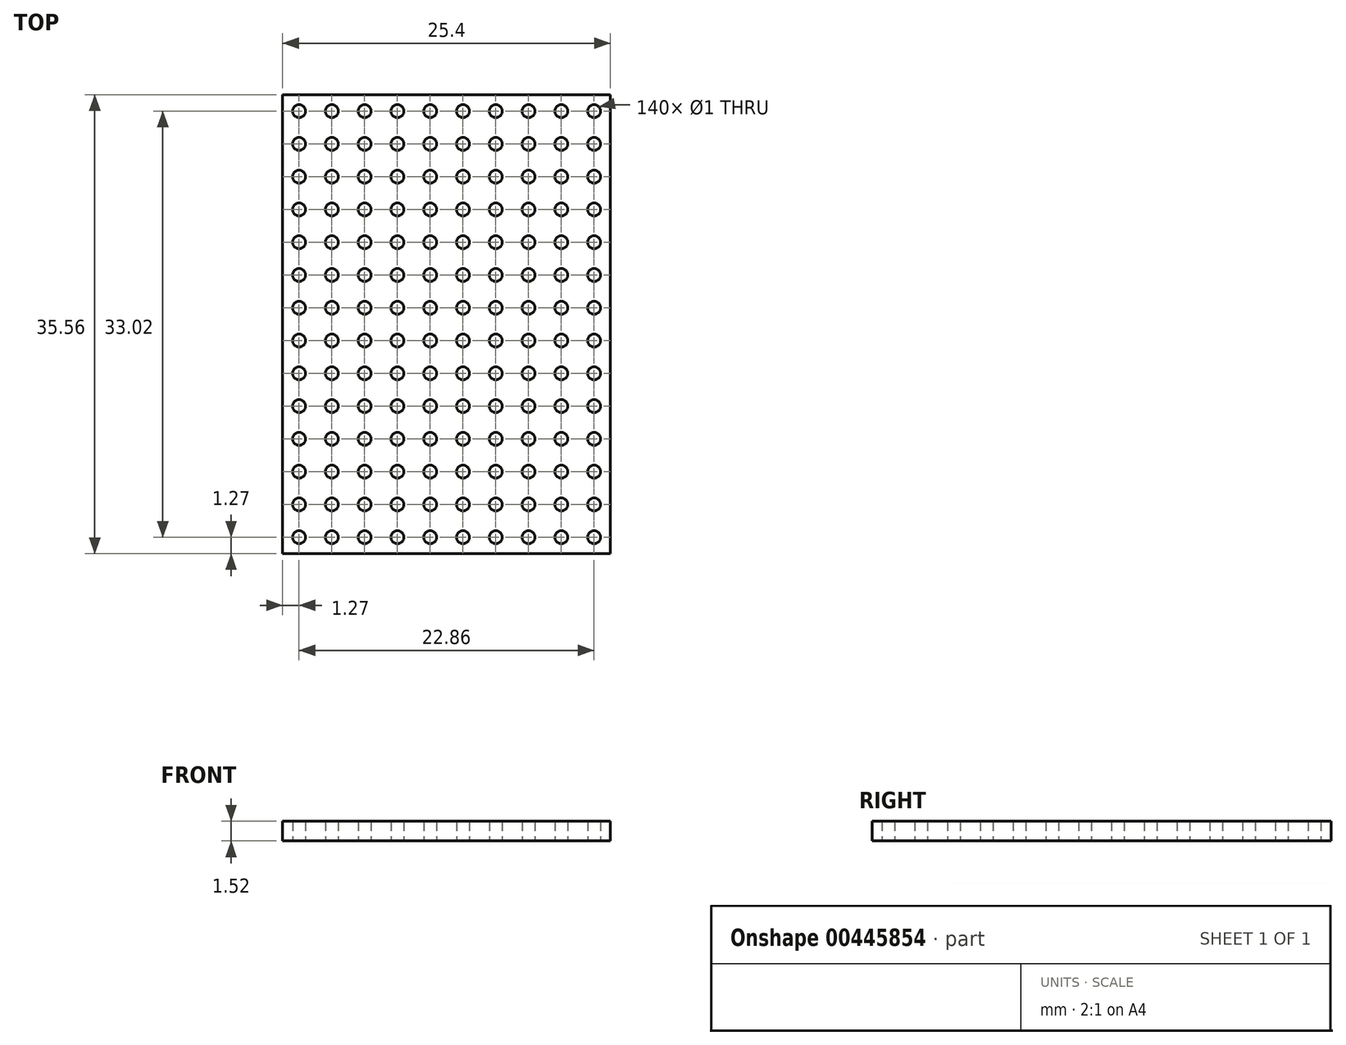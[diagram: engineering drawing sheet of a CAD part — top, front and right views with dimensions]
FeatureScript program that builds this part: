
annotation { "Feature Type Name" : "Feature", "Feature Type Description" : "" }
export const myFeature = defineFeature(function(context is Context, id is Id, definition is map)
    precondition{}
    {
        {
            var Q0;
            Q0=qCreatedBy(makeId("Top.planeOp"),FACE);
            var sketch = newSketch(context, id + "F0", { "sketchPlane" : qUnion([Q0])});
            skCircle(sketch, "E0", {"center": v(0, 0) * mm, "radius": 0.5 * mm});
            skCircle(sketch, "E1.0.1.0", {"center": v(0, 2.54) * mm, "radius": 0.5 * mm});
            skCircle(sketch, "E1.0.2.0", {"center": v(0, 5.08) * mm, "radius": 0.5 * mm});
            skCircle(sketch, "E1.0.3.0", {"center": v(0, 7.62) * mm, "radius": 0.5 * mm});
            skCircle(sketch, "E1.0.4.0", {"center": v(0, 10.16) * mm, "radius": 0.5 * mm});
            skCircle(sketch, "E1.0.5.0", {"center": v(0, 12.7) * mm, "radius": 0.5 * mm});
            skCircle(sketch, "E1.0.6.0", {"center": v(0, 15.24) * mm, "radius": 0.5 * mm});
            skCircle(sketch, "E1.0.7.0", {"center": v(0, 17.78) * mm, "radius": 0.5 * mm});
            skCircle(sketch, "E1.0.8.0", {"center": v(0, 20.32) * mm, "radius": 0.5 * mm});
            skCircle(sketch, "E1.0.9.0", {"center": v(0, 22.86) * mm, "radius": 0.5 * mm});
            skCircle(sketch, "E1.1.0.0", {"center": v(2.54, 0) * mm, "radius": 0.5 * mm});
            skCircle(sketch, "E1.1.1.0", {"center": v(2.54, 2.54) * mm, "radius": 0.5 * mm});
            skCircle(sketch, "E1.1.2.0", {"center": v(2.54, 5.08) * mm, "radius": 0.5 * mm});
            skCircle(sketch, "E1.1.3.0", {"center": v(2.54, 7.62) * mm, "radius": 0.5 * mm});
            skCircle(sketch, "E1.1.4.0", {"center": v(2.54, 10.16) * mm, "radius": 0.5 * mm});
            skCircle(sketch, "E1.1.5.0", {"center": v(2.54, 12.7) * mm, "radius": 0.5 * mm});
            skCircle(sketch, "E1.1.6.0", {"center": v(2.54, 15.24) * mm, "radius": 0.5 * mm});
            skCircle(sketch, "E1.1.7.0", {"center": v(2.54, 17.78) * mm, "radius": 0.5 * mm});
            skCircle(sketch, "E1.1.8.0", {"center": v(2.54, 20.32) * mm, "radius": 0.5 * mm});
            skCircle(sketch, "E1.1.9.0", {"center": v(2.54, 22.86) * mm, "radius": 0.5 * mm});
            skCircle(sketch, "E1.2.0.0", {"center": v(5.08, 0) * mm, "radius": 0.5 * mm});
            skCircle(sketch, "E1.2.1.0", {"center": v(5.08, 2.54) * mm, "radius": 0.5 * mm});
            skCircle(sketch, "E1.2.2.0", {"center": v(5.08, 5.08) * mm, "radius": 0.5 * mm});
            skCircle(sketch, "E1.2.3.0", {"center": v(5.08, 7.62) * mm, "radius": 0.5 * mm});
            skCircle(sketch, "E1.2.4.0", {"center": v(5.08, 10.16) * mm, "radius": 0.5 * mm});
            skCircle(sketch, "E1.2.5.0", {"center": v(5.08, 12.7) * mm, "radius": 0.5 * mm});
            skCircle(sketch, "E1.2.6.0", {"center": v(5.08, 15.24) * mm, "radius": 0.5 * mm});
            skCircle(sketch, "E1.2.7.0", {"center": v(5.08, 17.78) * mm, "radius": 0.5 * mm});
            skCircle(sketch, "E1.2.8.0", {"center": v(5.08, 20.32) * mm, "radius": 0.5 * mm});
            skCircle(sketch, "E1.2.9.0", {"center": v(5.08, 22.86) * mm, "radius": 0.5 * mm});
            skCircle(sketch, "E1.3.0.0", {"center": v(7.62, 0) * mm, "radius": 0.5 * mm});
            skCircle(sketch, "E1.3.1.0", {"center": v(7.62, 2.54) * mm, "radius": 0.5 * mm});
            skCircle(sketch, "E1.3.2.0", {"center": v(7.62, 5.08) * mm, "radius": 0.5 * mm});
            skCircle(sketch, "E1.3.3.0", {"center": v(7.62, 7.62) * mm, "radius": 0.5 * mm});
            skCircle(sketch, "E1.3.4.0", {"center": v(7.62, 10.16) * mm, "radius": 0.5 * mm});
            skCircle(sketch, "E1.3.5.0", {"center": v(7.62, 12.7) * mm, "radius": 0.5 * mm});
            skCircle(sketch, "E1.3.6.0", {"center": v(7.62, 15.24) * mm, "radius": 0.5 * mm});
            skCircle(sketch, "E1.3.7.0", {"center": v(7.62, 17.78) * mm, "radius": 0.5 * mm});
            skCircle(sketch, "E1.3.8.0", {"center": v(7.62, 20.32) * mm, "radius": 0.5 * mm});
            skCircle(sketch, "E1.3.9.0", {"center": v(7.62, 22.86) * mm, "radius": 0.5 * mm});
            skCircle(sketch, "E1.4.0.0", {"center": v(10.16, 0) * mm, "radius": 0.5 * mm});
            skCircle(sketch, "E1.4.1.0", {"center": v(10.16, 2.54) * mm, "radius": 0.5 * mm});
            skCircle(sketch, "E1.4.2.0", {"center": v(10.16, 5.08) * mm, "radius": 0.5 * mm});
            skCircle(sketch, "E1.4.3.0", {"center": v(10.16, 7.62) * mm, "radius": 0.5 * mm});
            skCircle(sketch, "E1.4.4.0", {"center": v(10.16, 10.16) * mm, "radius": 0.5 * mm});
            skCircle(sketch, "E1.4.5.0", {"center": v(10.16, 12.7) * mm, "radius": 0.5 * mm});
            skCircle(sketch, "E1.4.6.0", {"center": v(10.16, 15.24) * mm, "radius": 0.5 * mm});
            skCircle(sketch, "E1.4.7.0", {"center": v(10.16, 17.78) * mm, "radius": 0.5 * mm});
            skCircle(sketch, "E1.4.8.0", {"center": v(10.16, 20.32) * mm, "radius": 0.5 * mm});
            skCircle(sketch, "E1.4.9.0", {"center": v(10.16, 22.86) * mm, "radius": 0.5 * mm});
            skCircle(sketch, "E1.5.0.0", {"center": v(12.7, 0) * mm, "radius": 0.5 * mm});
            skCircle(sketch, "E1.5.1.0", {"center": v(12.7, 2.54) * mm, "radius": 0.5 * mm});
            skCircle(sketch, "E1.5.2.0", {"center": v(12.7, 5.08) * mm, "radius": 0.5 * mm});
            skCircle(sketch, "E1.5.3.0", {"center": v(12.7, 7.62) * mm, "radius": 0.5 * mm});
            skCircle(sketch, "E1.5.4.0", {"center": v(12.7, 10.16) * mm, "radius": 0.5 * mm});
            skCircle(sketch, "E1.5.5.0", {"center": v(12.7, 12.7) * mm, "radius": 0.5 * mm});
            skCircle(sketch, "E1.5.6.0", {"center": v(12.7, 15.24) * mm, "radius": 0.5 * mm});
            skCircle(sketch, "E1.5.7.0", {"center": v(12.7, 17.78) * mm, "radius": 0.5 * mm});
            skCircle(sketch, "E1.5.8.0", {"center": v(12.7, 20.32) * mm, "radius": 0.5 * mm});
            skCircle(sketch, "E1.5.9.0", {"center": v(12.7, 22.86) * mm, "radius": 0.5 * mm});
            skCircle(sketch, "E1.6.0.0", {"center": v(15.24, 0) * mm, "radius": 0.5 * mm});
            skCircle(sketch, "E1.6.1.0", {"center": v(15.24, 2.54) * mm, "radius": 0.5 * mm});
            skCircle(sketch, "E1.6.2.0", {"center": v(15.24, 5.08) * mm, "radius": 0.5 * mm});
            skCircle(sketch, "E1.6.3.0", {"center": v(15.24, 7.62) * mm, "radius": 0.5 * mm});
            skCircle(sketch, "E1.6.4.0", {"center": v(15.24, 10.16) * mm, "radius": 0.5 * mm});
            skCircle(sketch, "E1.6.5.0", {"center": v(15.24, 12.7) * mm, "radius": 0.5 * mm});
            skCircle(sketch, "E1.6.6.0", {"center": v(15.24, 15.24) * mm, "radius": 0.5 * mm});
            skCircle(sketch, "E1.6.7.0", {"center": v(15.24, 17.78) * mm, "radius": 0.5 * mm});
            skCircle(sketch, "E1.6.8.0", {"center": v(15.24, 20.32) * mm, "radius": 0.5 * mm});
            skCircle(sketch, "E1.6.9.0", {"center": v(15.24, 22.86) * mm, "radius": 0.5 * mm});
            skCircle(sketch, "E1.7.0.0", {"center": v(17.78, 0) * mm, "radius": 0.5 * mm});
            skCircle(sketch, "E1.7.1.0", {"center": v(17.78, 2.54) * mm, "radius": 0.5 * mm});
            skCircle(sketch, "E1.7.2.0", {"center": v(17.78, 5.08) * mm, "radius": 0.5 * mm});
            skCircle(sketch, "E1.7.3.0", {"center": v(17.78, 7.62) * mm, "radius": 0.5 * mm});
            skCircle(sketch, "E1.7.4.0", {"center": v(17.78, 10.16) * mm, "radius": 0.5 * mm});
            skCircle(sketch, "E1.7.5.0", {"center": v(17.78, 12.7) * mm, "radius": 0.5 * mm});
            skCircle(sketch, "E1.7.6.0", {"center": v(17.78, 15.24) * mm, "radius": 0.5 * mm});
            skCircle(sketch, "E1.7.7.0", {"center": v(17.78, 17.78) * mm, "radius": 0.5 * mm});
            skCircle(sketch, "E1.7.8.0", {"center": v(17.78, 20.32) * mm, "radius": 0.5 * mm});
            skCircle(sketch, "E1.7.9.0", {"center": v(17.78, 22.86) * mm, "radius": 0.5 * mm});
            skCircle(sketch, "E1.8.0.0", {"center": v(20.32, 0) * mm, "radius": 0.5 * mm});
            skCircle(sketch, "E1.8.1.0", {"center": v(20.32, 2.54) * mm, "radius": 0.5 * mm});
            skCircle(sketch, "E1.8.2.0", {"center": v(20.32, 5.08) * mm, "radius": 0.5 * mm});
            skCircle(sketch, "E1.8.3.0", {"center": v(20.32, 7.62) * mm, "radius": 0.5 * mm});
            skCircle(sketch, "E1.8.4.0", {"center": v(20.32, 10.16) * mm, "radius": 0.5 * mm});
            skCircle(sketch, "E1.8.5.0", {"center": v(20.32, 12.7) * mm, "radius": 0.5 * mm});
            skCircle(sketch, "E1.8.6.0", {"center": v(20.32, 15.24) * mm, "radius": 0.5 * mm});
            skCircle(sketch, "E1.8.7.0", {"center": v(20.32, 17.78) * mm, "radius": 0.5 * mm});
            skCircle(sketch, "E1.8.8.0", {"center": v(20.32, 20.32) * mm, "radius": 0.5 * mm});
            skCircle(sketch, "E1.8.9.0", {"center": v(20.32, 22.86) * mm, "radius": 0.5 * mm});
            skCircle(sketch, "E1.9.0.0", {"center": v(22.86, 0) * mm, "radius": 0.5 * mm});
            skCircle(sketch, "E1.9.1.0", {"center": v(22.86, 2.54) * mm, "radius": 0.5 * mm});
            skCircle(sketch, "E1.9.2.0", {"center": v(22.86, 5.08) * mm, "radius": 0.5 * mm});
            skCircle(sketch, "E1.9.3.0", {"center": v(22.86, 7.62) * mm, "radius": 0.5 * mm});
            skCircle(sketch, "E1.9.4.0", {"center": v(22.86, 10.16) * mm, "radius": 0.5 * mm});
            skCircle(sketch, "E1.9.5.0", {"center": v(22.86, 12.7) * mm, "radius": 0.5 * mm});
            skCircle(sketch, "E1.9.6.0", {"center": v(22.86, 15.24) * mm, "radius": 0.5 * mm});
            skCircle(sketch, "E1.9.7.0", {"center": v(22.86, 17.78) * mm, "radius": 0.5 * mm});
            skCircle(sketch, "E1.9.8.0", {"center": v(22.86, 20.32) * mm, "radius": 0.5 * mm});
            skCircle(sketch, "E1.9.9.0", {"center": v(22.86, 22.86) * mm, "radius": 0.5 * mm});
            skLineSegment(sketch, "E1.direction1", {"start": v(0, 0) * mm, "end": v(2.54, 0) * mm, "construction": true});
            skLineSegment(sketch, "E1.direction2", {"start": v(0, 0) * mm, "end": v(0, 2.54) * mm, "construction": true});
            skLineSegment(sketch, "E2.bottom", {"start": v(-1.27, -1.27) * mm, "end": v(24.13, -1.27) * mm});
            skLineSegment(sketch, "E2.top", {"start": v(-1.27, 34.3) * mm, "end": v(24.13, 34.3) * mm});
            skLineSegment(sketch, "E2.left", {"start": v(-1.27, -1.27) * mm, "end": v(-1.27, 34.3) * mm});
            skLineSegment(sketch, "E2.right", {"start": v(24.13, -1.27) * mm, "end": v(24.13, 34.3) * mm});
            skCircle(sketch, "E3.0.0.10", {"center": v(0, 25.4) * mm, "radius": 0.5 * mm});
            skCircle(sketch, "E3.0.0.11", {"center": v(0, 27.94) * mm, "radius": 0.5 * mm});
            skCircle(sketch, "E3.0.0.12", {"center": v(0, 30.48) * mm, "radius": 0.5 * mm});
            skCircle(sketch, "E3.0.0.13", {"center": v(0, 33.02) * mm, "radius": 0.5 * mm});
            skCircle(sketch, "E3.0.1.10", {"center": v(2.54, 25.4) * mm, "radius": 0.5 * mm});
            skCircle(sketch, "E3.0.1.11", {"center": v(2.54, 27.94) * mm, "radius": 0.5 * mm});
            skCircle(sketch, "E3.0.1.12", {"center": v(2.54, 30.48) * mm, "radius": 0.5 * mm});
            skCircle(sketch, "E3.0.1.13", {"center": v(2.54, 33.02) * mm, "radius": 0.5 * mm});
            skCircle(sketch, "E3.0.2.10", {"center": v(5.08, 25.4) * mm, "radius": 0.5 * mm});
            skCircle(sketch, "E3.0.2.11", {"center": v(5.08, 27.94) * mm, "radius": 0.5 * mm});
            skCircle(sketch, "E3.0.2.12", {"center": v(5.08, 30.48) * mm, "radius": 0.5 * mm});
            skCircle(sketch, "E3.0.2.13", {"center": v(5.08, 33.02) * mm, "radius": 0.5 * mm});
            skCircle(sketch, "E3.0.3.10", {"center": v(7.62, 25.4) * mm, "radius": 0.5 * mm});
            skCircle(sketch, "E3.0.3.11", {"center": v(7.62, 27.94) * mm, "radius": 0.5 * mm});
            skCircle(sketch, "E3.0.3.12", {"center": v(7.62, 30.48) * mm, "radius": 0.5 * mm});
            skCircle(sketch, "E3.0.3.13", {"center": v(7.62, 33.02) * mm, "radius": 0.5 * mm});
            skCircle(sketch, "E3.0.4.10", {"center": v(10.16, 25.4) * mm, "radius": 0.5 * mm});
            skCircle(sketch, "E3.0.4.11", {"center": v(10.16, 27.94) * mm, "radius": 0.5 * mm});
            skCircle(sketch, "E3.0.4.12", {"center": v(10.16, 30.48) * mm, "radius": 0.5 * mm});
            skCircle(sketch, "E3.0.4.13", {"center": v(10.16, 33.02) * mm, "radius": 0.5 * mm});
            skCircle(sketch, "E3.0.5.10", {"center": v(12.7, 25.4) * mm, "radius": 0.5 * mm});
            skCircle(sketch, "E3.0.5.11", {"center": v(12.7, 27.94) * mm, "radius": 0.5 * mm});
            skCircle(sketch, "E3.0.5.12", {"center": v(12.7, 30.48) * mm, "radius": 0.5 * mm});
            skCircle(sketch, "E3.0.5.13", {"center": v(12.7, 33.02) * mm, "radius": 0.5 * mm});
            skCircle(sketch, "E3.0.6.10", {"center": v(15.24, 25.4) * mm, "radius": 0.5 * mm});
            skCircle(sketch, "E3.0.6.11", {"center": v(15.24, 27.94) * mm, "radius": 0.5 * mm});
            skCircle(sketch, "E3.0.6.12", {"center": v(15.24, 30.48) * mm, "radius": 0.5 * mm});
            skCircle(sketch, "E3.0.6.13", {"center": v(15.24, 33.02) * mm, "radius": 0.5 * mm});
            skCircle(sketch, "E3.0.7.10", {"center": v(17.78, 25.4) * mm, "radius": 0.5 * mm});
            skCircle(sketch, "E3.0.7.11", {"center": v(17.78, 27.94) * mm, "radius": 0.5 * mm});
            skCircle(sketch, "E3.0.7.12", {"center": v(17.78, 30.48) * mm, "radius": 0.5 * mm});
            skCircle(sketch, "E3.0.7.13", {"center": v(17.78, 33.02) * mm, "radius": 0.5 * mm});
            skCircle(sketch, "E3.0.8.10", {"center": v(20.32, 25.4) * mm, "radius": 0.5 * mm});
            skCircle(sketch, "E3.0.8.11", {"center": v(20.32, 27.94) * mm, "radius": 0.5 * mm});
            skCircle(sketch, "E3.0.8.12", {"center": v(20.32, 30.48) * mm, "radius": 0.5 * mm});
            skCircle(sketch, "E3.0.8.13", {"center": v(20.32, 33.02) * mm, "radius": 0.5 * mm});
            skCircle(sketch, "E3.0.9.10", {"center": v(22.86, 25.4) * mm, "radius": 0.5 * mm});
            skCircle(sketch, "E3.0.9.11", {"center": v(22.86, 27.94) * mm, "radius": 0.5 * mm});
            skCircle(sketch, "E3.0.9.12", {"center": v(22.86, 30.48) * mm, "radius": 0.5 * mm});
            skCircle(sketch, "E3.0.9.13", {"center": v(22.86, 33.02) * mm, "radius": 0.5 * mm});
            skSolve(sketch);
        }
        {
            var Q0;
            Q0=makeQuery(id+"F0.imprint","IMPRINT",FACE,{"disambiguationData":[TD([[makeQuery(id+"F0.imprint","IMPRINT",EDGE,{"derivedFrom":sQuery(id+"F0.wireOp",EDGE,"E0")}),-1.0]])]});
            extrude(context, id + "F1", {"entities" : qUnion([Q0]), "depth" : 1.52 * mm});
        }
    });
